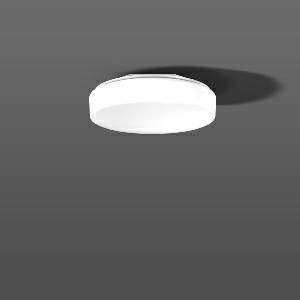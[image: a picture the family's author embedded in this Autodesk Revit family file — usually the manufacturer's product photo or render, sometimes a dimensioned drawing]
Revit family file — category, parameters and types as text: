
# Revit family: flat_polymero_kreis_672092_002_8_1_69be
name_source: partatom
category: Lighting Fixtures
units: mm (PartAtom-declared; Revit-internal decimal feet)

## family parameters
Cut with Voids When Loaded = No
Host = Face
Light Source = No
Part Type = Normal
Room Calculation Point = No
Round Connector Dimension = Use Diameter
Shared = No

## types (1)
- FLAT POLYMERO KREIS (1 x LED Modul 830, 1750 lm, 3000)
    Apparent Load = 15 VA
    CIE Flux Codes = 43 73 91 87 100
    Color Rendering = 80
    Color Temperature = 3000
    Default Elevation = 1800 mm
    Description = Series: FLAT POLYMERO KREIS
Decorative round surface-mounted luminaire. For escape route illumination. Base: metal, powder-coated. Diffuser made of plastic (polycarbonate), opal, shockproof. Diffuser fastening: patented push system. Suitable for Ceiling mounting, Wall (surface). Betriebsgeräte integriert. Einzelbatteriesystem mit automatischem Selbsttest. 
Colour: white
Diameter: 360 mm
Height: 109 mm
Weight: 1.87 kg
Operating mode: Combined NL readiness
Duration time: 3 h
Lamp: LED
Socket: without socket
Colour temperature: 3000K
Colour rendering index (CRI): 80
System power: 15 W
Rated luminous flux: 1750 lm
Luminous flux, emergency: 200 lm
System power, emergency: -
Control gear: Regulated power supply
Protection class: I
Type of protection: IP 40
    Height = 109 mm
    Lamp = 1 x LED Modul 830
    Lamp Light Flux = 1750 lm
    Lamp count = 1
    Length = 360 mm
    Lifetime = 50000 h
    Luminous efficacy = 117 lm/W
    Manufacturer = RZB
    ModVariant = No
    Model = 672092.002.8.1
    Mounting Place = Ceiling
    Mounting Type = Surface mounted
    Number of Poles = 1
    OnlyDefault = Yes
    Power Factor = 1
    Product Name = FLAT POLYMERO KREIS
    Product group = Surface mounted ceiling and wall luminaires
    ProductGroupID = 305
    Protection Class = Protection class I
    Protection Degree = Degree of protection
    RLX_Detail_Level = 1
    RLX_Emergency_Light_Flux = 200 lm
    RLX_Emergency_Type = 3
    RLX_Emergency_Type_DB = Yes
    RlxData = <blob elided: 52313 chars, md5=43a5f041>
    Socket = socket
    Standby Power = 0 W
    System Light Flux = 1750 lm
    System Power = 15 W
    Type Comments = Product without accessories
    Type Image = 672092.002.1.jpg
    URL = http://relux.com
    VarID = ---
    Voltage = 0 V
    Weight = 0.00 kg
    Width = 0 mm  [stored 0 ft]

note: [stored X ft] marks values corroborated as IEEE doubles in the binary element streams (Revit-internal decimal feet)

## geometry (parser evidence)
native form markers: Blend x4, Sweep x15
no freeform markers — native parametric forms only
